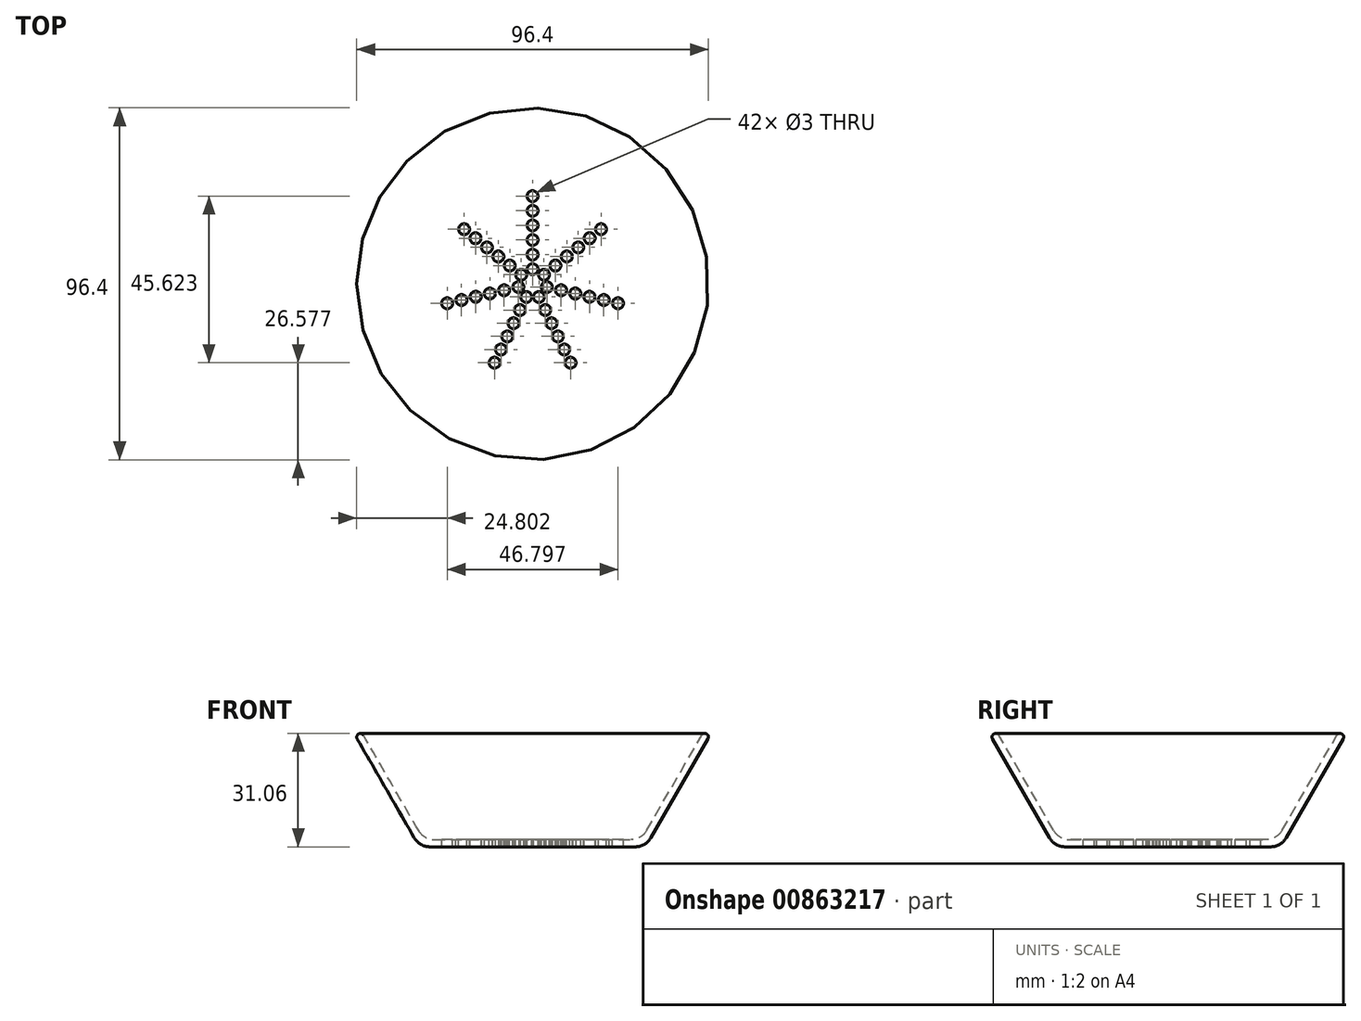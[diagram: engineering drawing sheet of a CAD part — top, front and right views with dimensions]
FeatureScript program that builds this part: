
annotation { "Feature Type Name" : "Feature", "Feature Type Description" : "" }
export const myFeature = defineFeature(function(context is Context, id is Id, definition is map)
    precondition{}
    {
        {
            var Q0;
            Q0=qCreatedBy(makeId("Front.planeOp"),FACE);
            var sketch = newSketch(context, id + "F0", { "sketchPlane" : qUnion([Q0])});
            skLineSegment(sketch, "E0", {"start": v(0, 0) * mm, "end": v(26.96, 0) * mm});
            skLineSegment(sketch, "E1", {"start": v(31.29, 2.5) * mm, "end": v(46.33, 28.56) * mm});
            skLineSegment(sketch, "E2.0", {"start": v(32.44, 0.5) * mm, "end": v(48.06, 27.56) * mm});
            skLineSegment(sketch, "E2.1", {"start": v(0, -2) * mm, "end": v(28.11, -2) * mm});
            skLineSegment(sketch, "E3", {"start": v(47.81, 28.85) * mm, "end": v(47.81, 28.85) * mm});
            skLineSegment(sketch, "E4", {"start": v(0, -2) * mm, "end": v(0, 47.87) * mm});
            skPoint(sketch, "E5.visualSharp", {"position": v(31, -2) * mm});
            skArc(sketch, "E5.filletArc", {"start": v(28.11, -2) * mm, "mid": v(30.61, -1.33) * mm, "end": v(32.44, 0.5) * mm});
            skPoint(sketch, "E6.visualSharp", {"position": v(29.85, 0) * mm});
            skArc(sketch, "E6.filletArc", {"start": v(26.96, 0) * mm, "mid": v(29.46, 0.67) * mm, "end": v(31.29, 2.5) * mm});
            skPoint(sketch, "E7.visualSharp", {"position": v(48.5, 28.31) * mm});
            skArc(sketch, "E7.filletArc", {"start": v(48.06, 27.56) * mm, "mid": v(48.18, 28.25) * mm, "end": v(47.81, 28.85) * mm});
            skPoint(sketch, "E8.visualSharp", {"position": v(46.9, 29.55) * mm});
            skArc(sketch, "E8.filletArc", {"start": v(47.81, 28.85) * mm, "mid": v(47, 29.04) * mm, "end": v(46.33, 28.56) * mm});
            skSolve(sketch);
        }
        {
            var Q0;
            Q0=qSketchRegion(id+"F0",true);
            var Q1;
            Q1=sQuery(id+"F0.wireOp",EDGE,"E4");
            revolve(context, id + "F1", {"surfaceOperationType" : NewSurfaceOperationType.NEW, "entities" : qUnion([Q0]), "axis" : qUnion([Q1]), "revolveType" : RevolveType.FULL});
        }
        {
            var Q0;
            Q0=makeQuery(id+"F1.opRevolve","SWEPT_FACE",FACE,{"disambiguationData":[OSD([sQuery(id+"F0.wireOp",EDGE,"E0")])]});
            var sketch = newSketch(context, id + "F2", { "sketchPlane" : qUnion([Q0])});
            skCircle(sketch, "E9", {"center": v(0, 20) * mm, "radius": 1.5 * mm});
            skCircle(sketch, "E10", {"center": v(0, 16) * mm, "radius": 1.5 * mm});
            skCircle(sketch, "E11", {"center": v(0, 12) * mm, "radius": 1.5 * mm});
            skCircle(sketch, "E12", {"center": v(0, 8) * mm, "radius": 1.5 * mm});
            skCircle(sketch, "E13", {"center": v(0, 4) * mm, "radius": 1.5 * mm});
            skCircle(sketch, "E14", {"center": v(0, 24) * mm, "radius": 1.5 * mm});
            skCircle(sketch, "E15.1.0", {"center": v(-18.76, 14.96) * mm, "radius": 1.5 * mm});
            skCircle(sketch, "E15.1.1", {"center": v(-15.64, 12.47) * mm, "radius": 1.5 * mm});
            skCircle(sketch, "E15.1.2", {"center": v(-12.5, 9.98) * mm, "radius": 1.5 * mm});
            skCircle(sketch, "E15.1.3", {"center": v(-9.38, 7.48) * mm, "radius": 1.5 * mm});
            skCircle(sketch, "E15.1.4", {"center": v(-6.25, 4.99) * mm, "radius": 1.5 * mm});
            skCircle(sketch, "E15.1.5", {"center": v(-3.13, 2.5) * mm, "radius": 1.5 * mm});
            skCircle(sketch, "E15.2.0", {"center": v(-23.4, -5.34) * mm, "radius": 1.5 * mm});
            skCircle(sketch, "E15.2.1", {"center": v(-19.5, -4.45) * mm, "radius": 1.5 * mm});
            skCircle(sketch, "E15.2.2", {"center": v(-15.6, -3.56) * mm, "radius": 1.5 * mm});
            skCircle(sketch, "E15.2.3", {"center": v(-11.7, -2.67) * mm, "radius": 1.5 * mm});
            skCircle(sketch, "E15.2.4", {"center": v(-7.8, -1.78) * mm, "radius": 1.5 * mm});
            skCircle(sketch, "E15.2.5", {"center": v(-3.9, -0.9) * mm, "radius": 1.5 * mm});
            skPoint(sketch, "E15.center", {"position": v(0, 0) * mm});
            skCircle(sketch, "E16.1.3.0", {"center": v(-10.41, -21.62) * mm, "radius": 1.5 * mm});
            skCircle(sketch, "E16.2.3.0", {"center": v(-8.68, -18.02) * mm, "radius": 1.5 * mm});
            skCircle(sketch, "E16.4.3.0", {"center": v(-6.94, -14.42) * mm, "radius": 1.5 * mm});
            skCircle(sketch, "E16.6.3.0", {"center": v(-5.2, -10.81) * mm, "radius": 1.5 * mm});
            skCircle(sketch, "E16.8.3.0", {"center": v(-3.47, -7.2) * mm, "radius": 1.5 * mm});
            skCircle(sketch, "E16.10.3.0", {"center": v(-1.74, -3.6) * mm, "radius": 1.5 * mm});
            skCircle(sketch, "E16.1.4.0", {"center": v(10.41, -21.62) * mm, "radius": 1.5 * mm});
            skCircle(sketch, "E16.2.4.0", {"center": v(8.68, -18.02) * mm, "radius": 1.5 * mm});
            skCircle(sketch, "E16.4.4.0", {"center": v(6.94, -14.42) * mm, "radius": 1.5 * mm});
            skCircle(sketch, "E16.6.4.0", {"center": v(5.2, -10.81) * mm, "radius": 1.5 * mm});
            skCircle(sketch, "E16.8.4.0", {"center": v(3.47, -7.2) * mm, "radius": 1.5 * mm});
            skCircle(sketch, "E16.10.4.0", {"center": v(1.74, -3.6) * mm, "radius": 1.5 * mm});
            skCircle(sketch, "E16.1.5.0", {"center": v(23.4, -5.34) * mm, "radius": 1.5 * mm});
            skCircle(sketch, "E16.2.5.0", {"center": v(19.5, -4.45) * mm, "radius": 1.5 * mm});
            skCircle(sketch, "E16.4.5.0", {"center": v(15.6, -3.56) * mm, "radius": 1.5 * mm});
            skCircle(sketch, "E16.6.5.0", {"center": v(11.7, -2.67) * mm, "radius": 1.5 * mm});
            skCircle(sketch, "E16.8.5.0", {"center": v(7.8, -1.78) * mm, "radius": 1.5 * mm});
            skCircle(sketch, "E16.10.5.0", {"center": v(3.9, -0.9) * mm, "radius": 1.5 * mm});
            skCircle(sketch, "E17.1.6.0", {"center": v(18.76, 14.96) * mm, "radius": 1.5 * mm});
            skCircle(sketch, "E17.2.6.0", {"center": v(15.64, 12.47) * mm, "radius": 1.5 * mm});
            skCircle(sketch, "E17.4.6.0", {"center": v(12.5, 9.98) * mm, "radius": 1.5 * mm});
            skCircle(sketch, "E17.6.6.0", {"center": v(9.38, 7.48) * mm, "radius": 1.5 * mm});
            skCircle(sketch, "E17.8.6.0", {"center": v(6.25, 4.99) * mm, "radius": 1.5 * mm});
            skCircle(sketch, "E17.10.6.0", {"center": v(3.13, 2.5) * mm, "radius": 1.5 * mm});
            skSolve(sketch);
        }
        {
            var Q0;
            Q0=qSketchRegion(id+"F2",true);
            extrude(context, id + "F3", {"entities" : qUnion([Q0]), "operationType" : NewBodyOperationType.REMOVE, "oppositeDirection" : true, "depth" : 25 * mm, "offsetDistance" : 25 * mm});
        }
    });
